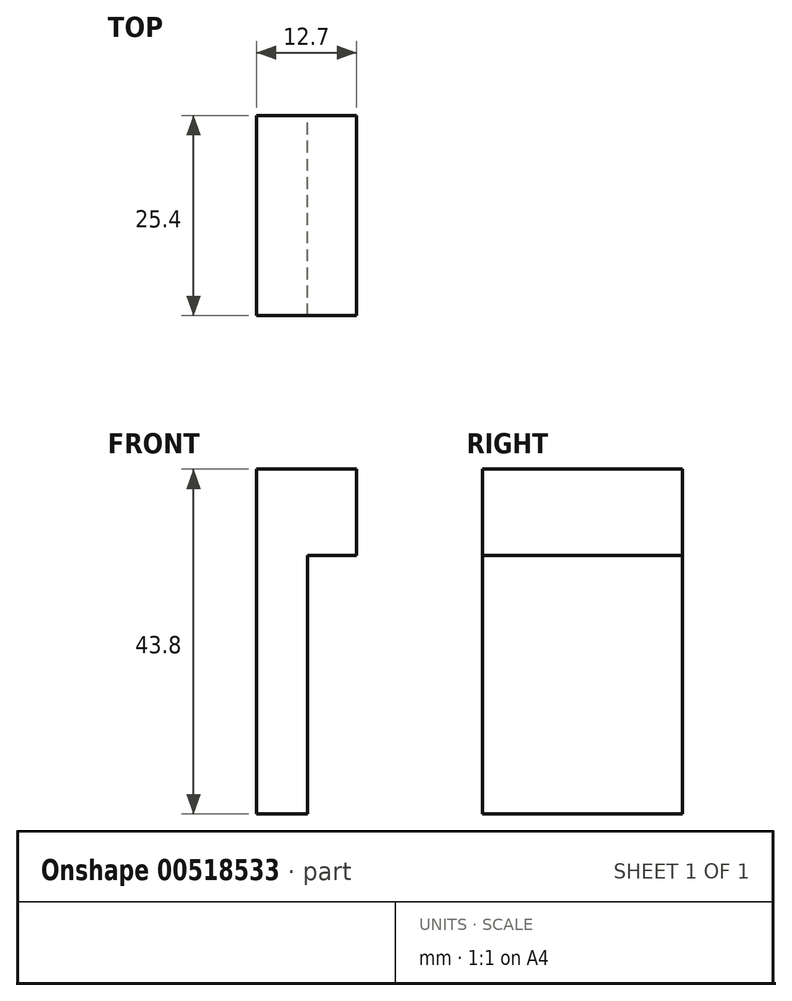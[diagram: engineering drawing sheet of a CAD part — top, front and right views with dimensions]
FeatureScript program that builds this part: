
annotation { "Feature Type Name" : "Feature", "Feature Type Description" : "" }
export const myFeature = defineFeature(function(context is Context, id is Id, definition is map)
    precondition{}
    {
        {
            var Q0;
            Q0=qCreatedBy(makeId("Front.planeOp"),FACE);
            var sketch = newSketch(context, id + "F0", { "sketchPlane" : qUnion([Q0])});
            skLineSegment(sketch, "E0", {"start": v(0, 0) * mm, "end": v(0, 43.8) * mm});
            skLineSegment(sketch, "E1", {"start": v(0, 43.8) * mm, "end": v(12.7, 43.8) * mm});
            skLineSegment(sketch, "E2", {"start": v(12.7, 43.8) * mm, "end": v(12.7, 32.8) * mm});
            skLineSegment(sketch, "E3", {"start": v(12.7, 32.8) * mm, "end": v(6.45, 32.8) * mm});
            skLineSegment(sketch, "E4", {"start": v(6.45, 32.8) * mm, "end": v(6.45, 0) * mm});
            skLineSegment(sketch, "E5", {"start": v(6.45, 0) * mm, "end": v(0, 0) * mm});
            skSolve(sketch);
        }
        {
            var Q0;
            Q0=makeQuery(id+"F0.imprint","IMPRINT",FACE,{"disambiguationData":[TD([[makeQuery(id+"F0.imprint","IMPRINT",EDGE,{"derivedFrom":sQuery(id+"F0.wireOp",EDGE,"E0")}),-1.0]])]});
            extrude(context, id + "F1", {"entities" : qUnion([Q0]), "depth" : 25.4 * mm, "offsetDistance" : 25.4 * mm});
        }
    });
